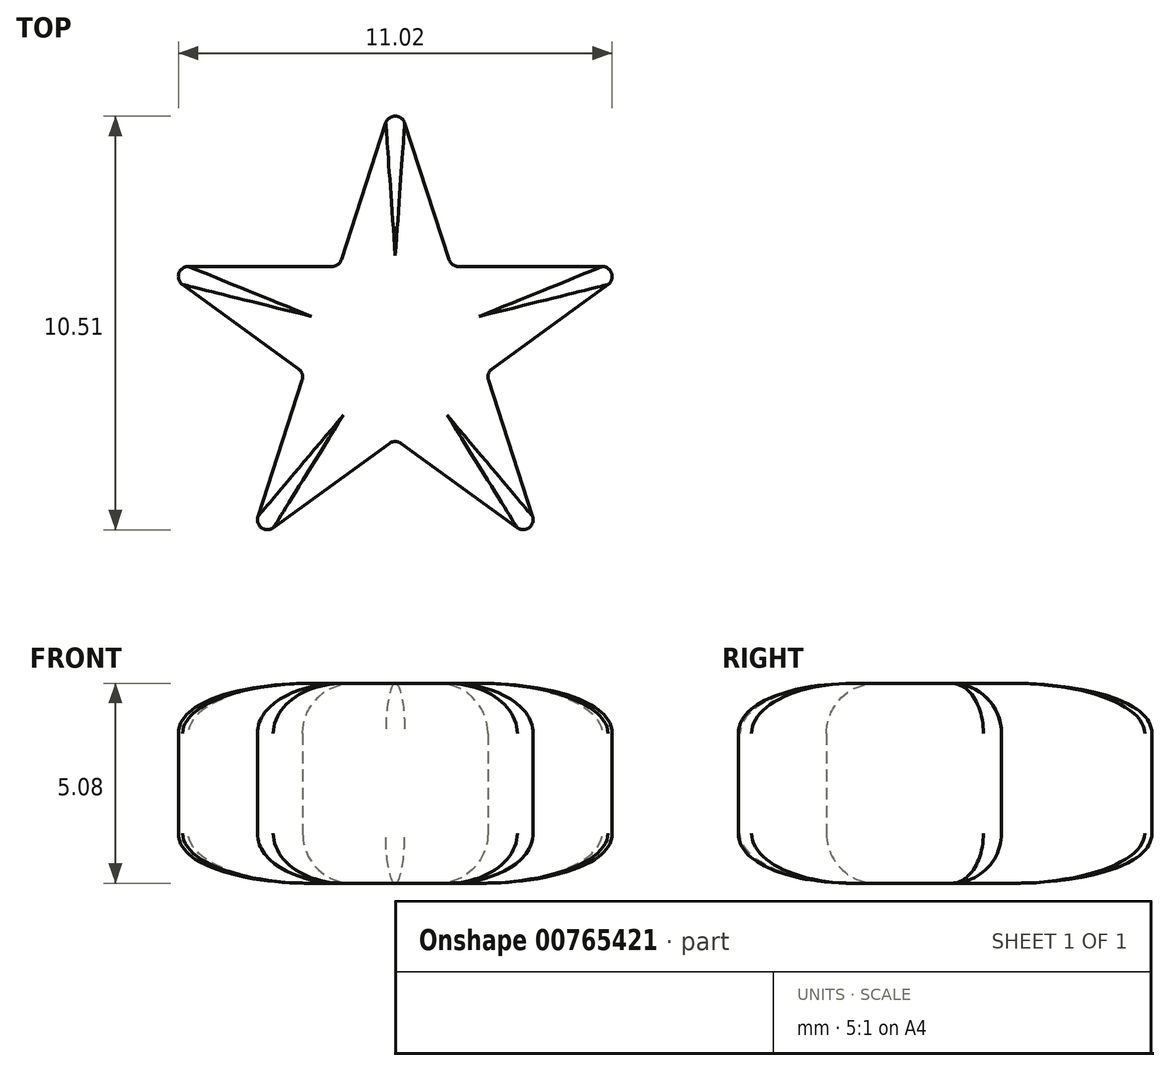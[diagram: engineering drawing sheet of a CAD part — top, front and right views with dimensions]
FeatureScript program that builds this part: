
annotation { "Feature Type Name" : "Feature", "Feature Type Description" : "" }
export const myFeature = defineFeature(function(context is Context, id is Id, definition is map)
    precondition{}
    {
        {
            var Q0;
            Q0=qCreatedBy(makeId("Top.planeOp"),FACE);
            var sketch = newSketch(context, id + "F0", { "sketchPlane" : qUnion([Q0])});
            skPoint(sketch, "E0", {"position": v(0, 0) * mm});
            skCircle(sketch, "E1", {"center": v(0, 0) * mm, "radius": 6.35 * mm});
            skCircle(sketch, "E2.cCircle", {"center": v(0, 0) * mm, "radius": 6.35 * mm, "construction": true});
            skLineSegment(sketch, "E2.0", {"start": v(0, 6.35) * mm, "end": v(6.04, 1.96) * mm});
            skLineSegment(sketch, "E2.1", {"start": v(6.04, 1.96) * mm, "end": v(3.73, -5.14) * mm});
            skLineSegment(sketch, "E2.2", {"start": v(3.73, -5.14) * mm, "end": v(-3.73, -5.14) * mm});
            skLineSegment(sketch, "E2.3", {"start": v(-3.73, -5.14) * mm, "end": v(-6.04, 1.96) * mm});
            skLineSegment(sketch, "E2.4", {"start": v(-6.04, 1.96) * mm, "end": v(0, 6.35) * mm});
            skLineSegment(sketch, "E3", {"start": v(-3.5, -4.4) * mm, "end": v(-2.36, -0.93) * mm});
            skLineSegment(sketch, "E4", {"start": v(0.24, 5.6) * mm, "end": v(1.37, 2.14) * mm});
            skLineSegment(sketch, "E5", {"start": v(3.1, -4.68) * mm, "end": v(0.15, -2.53) * mm});
            skLineSegment(sketch, "E6", {"start": v(-5.26, 1.96) * mm, "end": v(-1.61, 1.96) * mm});
            skLineSegment(sketch, "E7", {"start": v(5.4, 1.5) * mm, "end": v(2.46, -0.64) * mm});
            skLineSegment(sketch, "E8.trimOffspring", {"start": v(-1.37, 2.14) * mm, "end": v(-0.24, 5.6) * mm});
            skLineSegment(sketch, "E9.trimOffspring", {"start": v(-2.46, -0.64) * mm, "end": v(-5.4, 1.5) * mm});
            skLineSegment(sketch, "E10.trimOffspring", {"start": v(-0.15, -2.53) * mm, "end": v(-3.1, -4.68) * mm});
            skLineSegment(sketch, "E11.trimOffspring", {"start": v(2.36, -0.93) * mm, "end": v(3.5, -4.4) * mm});
            skLineSegment(sketch, "E12.trimOffspring", {"start": v(1.61, 1.96) * mm, "end": v(5.26, 1.96) * mm});
            skPoint(sketch, "E13.visualSharp", {"position": v(-6.04, 1.96) * mm});
            skArc(sketch, "E13.filletArc", {"start": v(-5.26, 1.96) * mm, "mid": v(-5.5, 1.79) * mm, "end": v(-5.4, 1.5) * mm});
            skPoint(sketch, "E14.visualSharp", {"position": v(-3.73, -5.14) * mm});
            skArc(sketch, "E14.filletArc", {"start": v(-3.5, -4.4) * mm, "mid": v(-3.4, -4.68) * mm, "end": v(-3.1, -4.68) * mm});
            skPoint(sketch, "E15.visualSharp", {"position": v(3.73, -5.14) * mm});
            skArc(sketch, "E15.filletArc", {"start": v(3.1, -4.68) * mm, "mid": v(3.4, -4.68) * mm, "end": v(3.5, -4.4) * mm});
            skPoint(sketch, "E16.visualSharp", {"position": v(6.04, 1.96) * mm});
            skArc(sketch, "E16.filletArc", {"start": v(5.4, 1.5) * mm, "mid": v(5.5, 1.79) * mm, "end": v(5.26, 1.96) * mm});
            skPoint(sketch, "E17.visualSharp", {"position": v(0, 6.35) * mm});
            skArc(sketch, "E17.filletArc", {"start": v(0.24, 5.6) * mm, "mid": v(0, 5.78) * mm, "end": v(-0.24, 5.6) * mm});
            skPoint(sketch, "E18.visualSharp", {"position": v(-1.43, 1.96) * mm});
            skArc(sketch, "E18.filletArc", {"start": v(-1.61, 1.96) * mm, "mid": v(-1.46, 2.01) * mm, "end": v(-1.37, 2.14) * mm});
            skPoint(sketch, "E19.visualSharp", {"position": v(-2.3, -0.75) * mm});
            skArc(sketch, "E19.filletArc", {"start": v(-2.36, -0.93) * mm, "mid": v(-2.36, -0.77) * mm, "end": v(-2.46, -0.64) * mm});
            skPoint(sketch, "E20.visualSharp", {"position": v(0, -2.43) * mm});
            skArc(sketch, "E20.filletArc", {"start": v(0.15, -2.53) * mm, "mid": v(0, -2.49) * mm, "end": v(-0.15, -2.53) * mm});
            skPoint(sketch, "E21.visualSharp", {"position": v(2.3, -0.75) * mm});
            skArc(sketch, "E21.filletArc", {"start": v(2.46, -0.64) * mm, "mid": v(2.36, -0.77) * mm, "end": v(2.36, -0.93) * mm});
            skPoint(sketch, "E22.visualSharp", {"position": v(1.43, 1.96) * mm});
            skArc(sketch, "E22.filletArc", {"start": v(1.37, 2.14) * mm, "mid": v(1.46, 2.01) * mm, "end": v(1.61, 1.96) * mm});
            skSolve(sketch);
        }
        {
            var Q0;
            Q0=makeQuery(id+"F0.imprint","IMPRINT",FACE,{"disambiguationData":[TD([[makeQuery(id+"F0.imprint","IMPRINT",EDGE,{"derivedFrom":sQuery(id+"F0.wireOp",EDGE,"E3")}),-1.0]])]});
            extrude(context, id + "F1", {"entities" : qUnion([Q0]), "depth" : 5.08 * mm, "offsetDistance" : 25.4 * mm});
        }
        {
            var Q0;
            Q0=makeQuery(id+"F1.opExtrude","CAP_EDGE",EDGE,{"disambiguationData":[OSD([sQuery(id+"F0.wireOp",EDGE,"E10.trimOffspring")])],"isStart":false});
            var Q1;
            Q1=makeQuery(id+"F1.opExtrude","CAP_EDGE",EDGE,{"disambiguationData":[OSD([sQuery(id+"F0.wireOp",EDGE,"E10.trimOffspring")])],"isStart":true});
            fillet(context, id + "F2", {"entities" : qUnion([Q0, Q1]), "radius" : 1.27 * mm, "tangentPropagation" : true, "allowEdgeOverflow" : false});
        }
    });
